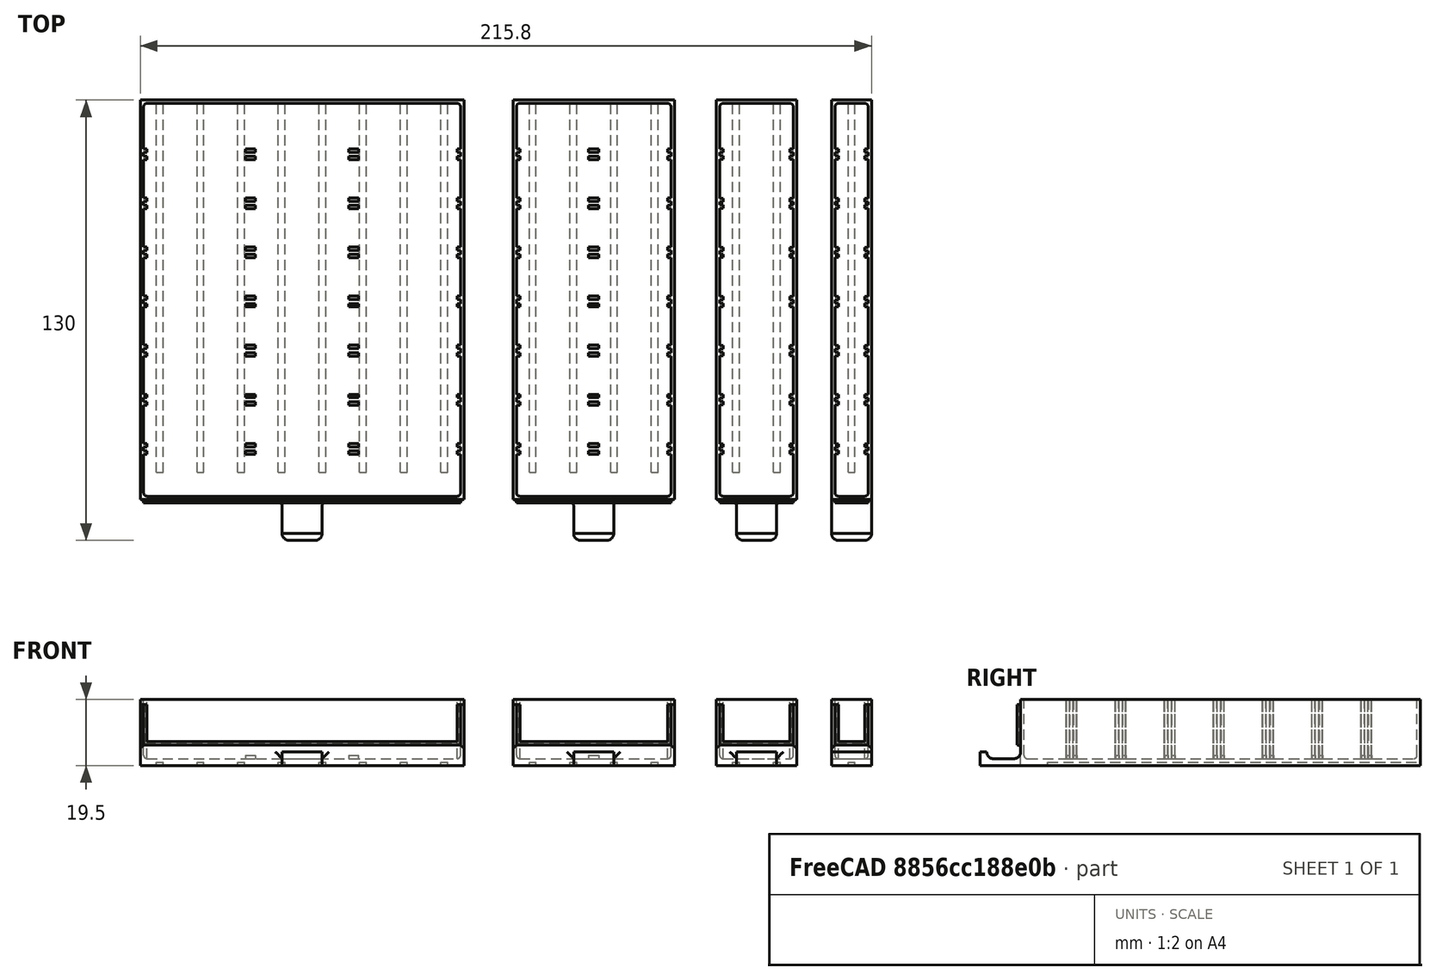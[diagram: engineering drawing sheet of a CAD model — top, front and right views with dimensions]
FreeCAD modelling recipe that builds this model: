
FCSTD DOCUMENT  (FreeCAD 0.16R)
Label: drawers
License: All rights reserved
LicenseURL: http://en.wikipedia.org/wiki/All_rights_reserved
objects: Part::Box×46, Part::Cut×23, Part::Fillet×20, Part::MultiFuse×19, Part::FeaturePython×8
note: 116 computed .brp shape members not serialized (recipe doc carries the construction recipe); baked Part::Feature solids carry a one-line shape summary decoded from their .brp

FEATURE [Part::Box] Box  label="outer_box"
  Height = 19.5
  Length = 95.5
  Width = 118
FEATURE [Part::Box] Box001  label="inner_box"
  Height = 18.5
  Length = 93.5
  Placement = pos=(1,1,2) rot=(0,0,1;0rad)
  Width = 116
FEATURE [Part::Fillet] Fillet
  Base = -> Box001
  Edges = 8 edges r=1: [Edge1,Edge3,Edge4,Edge5,Edge7,Edge8,Edge9,Edge11]
FEATURE [Part::Cut] Cut  label="Guideless Drawer"
  Base = -> Box
  Tool = -> Fillet
FEATURE [Part::Box] Box004  label="Guide"
  Height = 1
  Length = 2
  Placement = pos=(0,8,0) rot=(0,0,1;0rad)
  Width = 110
FEATURE [Part::FeaturePython] Array  label="Guide array"  # Draft array (typed FeaturePython)
  Angle = 360
  ArrayType = 0
  Axis = (0,0,1)
  Base = -> Box004
  Center = (0,0,0)
  Fuse = false
  IntervalAxis = (0,0,0)
  IntervalX = (12,0,0)
  IntervalY = (0,1,0)
  IntervalZ = (0,0,0)
  NumberPolar = 1
  NumberX = 8
  NumberY = 1
  NumberZ = 1
  Placement = pos=(4.75,0,0) rot=(0,0,1;0rad)
FEATURE [Part::Box] Box006  label="Separator Holder Block"
  Height = 17.5
  Length = 93.5
  Placement = pos=(1,13.4,2) rot=(0,0,1;0rad)
  Width = 3.2
FEATURE [Part::Box] Box007  label="Separator Gap"
  Height = 17.5
  Length = 93.5
  Placement = pos=(1,14.4,2) rot=(0,0,1;0rad)
  Width = 1.2
FEATURE [Part::Box] Box008  label="Separator Holder Gap Block"
  Height = 17.5
  Length = 91.5
  Placement = pos=(2,13.4,2) rot=(0,0,1;0rad)
  Width = 3.2
FEATURE [Part::Fillet] Fillet005
  Base = -> Box006
  Edges = 2 edges r=1: [Edge4,Edge8]
FEATURE [Part::Cut] Cut002  label="Separator Holder Guides"
  Base = -> Fillet005
  Tool = -> Box007
FEATURE [Part::Cut] Cut004  label="Handlerless Guided Drawer"
  Base = -> Cut
  Tool = -> Array
FEATURE [Part::Box] Box009  label="Bottom Separator Holder Gap Block"
  Height = 1
  Length = 3
  Placement = pos=(31,13.4,2) rot=(0,0,1;0rad)
  Width = 3.2
FEATURE [Part::FeaturePython] Array001  label="Bottom Separator Gap Array"  # Draft array (typed FeaturePython)
  Angle = 360
  ArrayType = 0
  Axis = (0,0,1)
  Base = -> Box009
  Center = (0,0,0)
  Fuse = false
  IntervalAxis = (0,0,0)
  IntervalX = (30.5,0,0)
  IntervalY = (0,1,0)
  IntervalZ = (0,0,0)
  NumberPolar = 1
  NumberX = 2
  NumberY = 1
  NumberZ = 1
FEATURE [Part::Cut] Cut005  label="Separator Holder Gap"
  Base = -> Box008
  Tool = -> Array001
FEATURE [Part::Cut] Cut006  label="Separator Holder"
  Base = -> Cut002
  Tool = -> Cut005
FEATURE [Part::FeaturePython] Array002  label="Separator Holder Array"  # Draft array (typed FeaturePython)
  Angle = 360
  ArrayType = 0
  Axis = (0,0,1)
  Base = -> Cut006
  Center = (0,0,0)
  Fuse = false
  IntervalAxis = (0,0,0)
  IntervalX = (1,0,0)
  IntervalY = (0,14.5,0)
  IntervalZ = (0,0,0)
  NumberPolar = 1
  NumberX = 1
  NumberY = 7
  NumberZ = 1
FEATURE [Part::Box] Box010  label="LabelHolder_Main_Block"
  Height = 12
  Length = 93.5
  Placement = pos=(1,-1,6) rot=(0,0,1;0rad)
  Width = 1
  expr: Placement.Base.y = outer_box.Placement.Base.y - LabelHolder_Main_Block.Width
  expr: Placement.Base.x = inner_box.Placement.Base.x
  expr: Length = inner_box.Length
FEATURE [Part::Box] Box011  label="LabelHolder_Inner_Gap"
  Height = 11.5
  Length = 92.5
  Placement = pos=(1.5,-0.5,6.5) rot=(0,0,1;0rad)
  Width = 0.5
  expr: Height = LabelHolder_Main_Block.Height - 0.5mm
  expr: Placement.Base.z = LabelHolder_Main_Block.Placement.Base.z + 0.5mm
  expr: Placement.Base.y = LabelHolder_Main_Block.Placement.Base.y + 0.5mm
  expr: Placement.Base.x = LabelHolder_Main_Block.Placement.Base.x + 0.5mm
  expr: Length = LabelHolder_Main_Block.Length - 1mm
FEATURE [Part::Box] Box012  label="LabelHolder_Outer_Gap"
  Height = 11
  Length = 91.5
  Placement = pos=(2,-1,7) rot=(0,0,1;0rad)
  Width = 0.5
  expr: Height = LabelHolder_Main_Block.Height - 1mm
  expr: Placement.Base.z = LabelHolder_Main_Block.Placement.Base.z + 1mm
  expr: Placement.Base.y = LabelHolder_Main_Block.Placement.Base.y
  expr: Placement.Base.x = LabelHolder_Main_Block.Placement.Base.x + 1mm
  expr: Length = LabelHolder_Main_Block.Length - 2mm
FEATURE [Part::MultiFuse] Fusion003  label="LabelHolder Gap"
  Shapes = -> [Box011,Box012]
FEATURE [Part::Cut] Cut007  label="LabelHolder"
  Base = -> Box010
  Tool = -> Fusion003
FEATURE [Part::MultiFuse] Fusion  label="Handlerless Drawer"
  Shapes = -> [Cut004,Array002]
FEATURE [Part::Box] Box013  label="Handler_block"
  Height = 2
  Length = 11.8
  Placement = pos=(41.85,-12,0) rot=(0,0,1;0rad)
  Width = 12
  expr: Placement.Base.y = outer_box.Placement.Base.y - Handler_block.Width
  expr: Placement.Base.x = outer_box.Placement.Base.x + (outer_box.Length - Handler_block.Length) / 2
FEATURE [Part::Box] Box015  label="Handler_pick"
  Height = 2
  Length = 11.8
  Placement = pos=(41.85,-12,2) rot=(0,0,1;0rad)
  Width = 2
  expr: Placement.Base.z = Handler_block.Placement.Base.z + 2mm
  expr: Placement.Base.y = Handler_block.Placement.Base.y
  expr: Placement.Base.x = Handler_block.Placement.Base.x
FEATURE [Part::MultiFuse] Fusion004
  Shapes = -> [Box015,Box013]
FEATURE [Part::Fillet] Fillet006
  Base = -> Fusion004
  Edges = 5 edges r=1.9: [Edge5,Edge8,Edge10,Edge13,Edge19]
FEATURE [Part::MultiFuse] Fusion005
  Shapes = -> [Fillet006,Fusion]
FEATURE [Part::Fillet] Fillet007  label="LabelHolderlessCabinet"
  Base = -> Fusion005
  Edges = 3 edges r=2: [Edge25,Edge34,Edge39]
FEATURE [Part::MultiFuse] Fusion006
  Shapes = -> [Cut007,Fillet007]
FEATURE [Part::Fillet] Fillet008  label="BigDrawer"
  Base = -> Fusion006
  Edges = 3 edges r=0.9: [Edge11,Edge27,Edge28]
FEATURE [Part::Box] Box016  label="outer_box001"
  Height = 19.5
  Length = 47.6
  Width = 118
FEATURE [Part::Box] Box017  label="inner_box001"
  Height = 18.5
  Length = 45.6
  Placement = pos=(1,1,2) rot=(0,0,1;0rad)
  Width = 116
FEATURE [Part::Fillet] Fillet009
  Base = -> Box017
  Edges = 8 edges r=1: [Edge1,Edge3,Edge4,Edge5,Edge7,Edge8,Edge9,Edge11]
FEATURE [Part::Cut] Cut008  label="Guideless drawer"
  Base = -> Box016
  Tool = -> Fillet009
FEATURE [Part::Box] Box018  label="Guide001"
  Height = 1
  Length = 2
  Placement = pos=(4.8,8,0) rot=(0,0,1;0rad)
  Width = 110
FEATURE [Part::FeaturePython] Array003  label="Guide Array"  # Draft array (typed FeaturePython)
  Angle = 360
  ArrayType = 0
  Axis = (0,0,1)
  Base = -> Box018
  Center = (0,0,0)
  Fuse = false
  IntervalAxis = (0,0,0)
  IntervalX = (12,0,0)
  IntervalY = (0,1,0)
  IntervalZ = (0,0,0)
  NumberPolar = 1
  NumberX = 4
  NumberY = 1
  NumberZ = 1
FEATURE [Part::Box] Box019  label="Separator Block"
  Height = 17.5
  Length = 45.6
  Placement = pos=(1,13.4,2) rot=(0,0,1;0rad)
  Width = 3.2
FEATURE [Part::Box] Box020  label="Separator Gap001"
  Height = 17.5
  Length = 45.6
  Placement = pos=(1,14.4,2) rot=(0,0,1;0rad)
  Width = 1.2
FEATURE [Part::Box] Box021  label="Separator Holder Gap Block001"
  Height = 17.5
  Length = 43.6
  Placement = pos=(2,13.4,2) rot=(0,0,1;0rad)
  Width = 3.2
FEATURE [Part::Fillet] Fillet010
  Base = -> Box019
  Edges = 2 edges r=1: [Edge4,Edge8]
FEATURE [Part::Cut] Cut009  label="Separator Holder Guides001"
  Base = -> Fillet010
  Tool = -> Box020
FEATURE [Part::Cut] Cut010  label="Separatorless Guided Drawer"
  Base = -> Cut008
  Tool = -> Array003
FEATURE [Part::Box] Box022  label="Bottom Separator Holder Gap Block001"
  Height = 1
  Length = 3
  Placement = pos=(22.3,13.4,2) rot=(0,0,1;0rad)
  Width = 3.2
FEATURE [Part::Cut] Cut011  label="Separator Holder Gap001"
  Base = -> Box021
  Tool = -> Box022
FEATURE [Part::Cut] Cut012  label="Separator Holder001"
  Base = -> Cut009
  Tool = -> Cut011
FEATURE [Part::FeaturePython] Array004  label="Separator Holder Array001"  # Draft array (typed FeaturePython)
  Angle = 360
  ArrayType = 0
  Axis = (0,0,1)
  Base = -> Cut012
  Center = (0,0,0)
  Fuse = false
  IntervalAxis = (0,0,0)
  IntervalX = (1,0,0)
  IntervalY = (0,14.5,0)
  IntervalZ = (0,0,0)
  NumberPolar = 1
  NumberX = 1
  NumberY = 7
  NumberZ = 1
FEATURE [Part::Box] Box023  label="LabelHolder_Main_Block001"
  Height = 12
  Length = 45.6
  Placement = pos=(1,-1,6) rot=(0,0,1;0rad)
  Width = 1
  expr: Placement.Base.y = outer_box.Placement.Base.y - LabelHolder_Main_Block.Width
  expr: Placement.Base.x = inner_box.Placement.Base.x
  expr: Length = inner_box.Length
FEATURE [Part::Box] Box024  label="LabelHolder_Inner_Gap001"
  Height = 11.5
  Length = 44.6
  Placement = pos=(1.5,-0.5,6.5) rot=(0,0,1;0rad)
  Width = 0.5
  expr: Placement.Base.y = LabelHolder_Main_Block.Placement.Base.y + 0.5mm
  expr: Height = LabelHolder_Main_Block.Height - 0.5mm
  expr: Placement.Base.z = LabelHolder_Main_Block.Placement.Base.z + 0.5mm
  expr: Length = inner_box.Length - 1mm
FEATURE [Part::Box] Box025  label="LabelHolder_Outer_Gap001"
  Height = 11
  Length = 43.6
  Placement = pos=(2,-1,7) rot=(0,0,1;0rad)
  Width = 0.5
  expr: Placement.Base.y = LabelHolder_Main_Block.Placement.Base.y
  expr: Placement.Base.x = LabelHolder_Main_Block.Placement.Base.x + 1mm
  expr: Length = LabelHolder_Main_Block.Length - 2mm
  expr: Height = LabelHolder_Main_Block.Height - 1mm
  expr: Placement.Base.z = LabelHolder_Main_Block.Placement.Base.z + 1mm
FEATURE [Part::MultiFuse] Fusion007  label="LabelHolder_Gap"
  Shapes = -> [Box024,Box025]
FEATURE [Part::Cut] Cut013  label="LabelHolder001"
  Base = -> Box023
  Tool = -> Fusion007
FEATURE [Part::MultiFuse] Fusion008  label="Handlerless Drawer001"
  Shapes = -> [Array004,Cut010]
FEATURE [Part::Box] Box026  label="Handler_block001"
  Height = 2
  Length = 11.8
  Placement = pos=(17.9,-12,0) rot=(0,0,1;0rad)
  Width = 12
  expr: Placement.Base.y = outer_box.Placement.Base.y - Handler_block.Width
  expr: Placement.Base.x = outer_box.Placement.Base.x + (outer_box.Length - Handler_block.Length) / 2
FEATURE [Part::Box] Box027  label="Handler_pick001"
  Height = 2
  Length = 11.8
  Placement = pos=(17.9,-12,2) rot=(0,0,1;0rad)
  Width = 2
  expr: Placement.Base.z = Handler_block.Placement.Base.z + 2mm
  expr: Placement.Base.y = Handler_block.Placement.Base.y
  expr: Placement.Base.x = Handler_block.Placement.Base.x
FEATURE [Part::MultiFuse] Fusion009
  Shapes = -> [Box026,Box027]
FEATURE [Part::Fillet] Fillet011
  Base = -> Fusion009
  Edges = 5 edges r=1.9: [Edge5,Edge11,Edge15,Edge18,Edge19]
FEATURE [Part::MultiFuse] Fusion010
  Shapes = -> [Fusion008,Fillet011]
FEATURE [Part::Fillet] Fillet012
  Base = -> Fusion010
  Edges = 3 edges r=2: [Edge627,Edge628,Edge629]
FEATURE [Part::MultiFuse] Fusion011
  Shapes = -> [Fillet012,Cut013]
FEATURE [Part::Fillet] Fillet013  label="StandardDrawer"
  Base = -> Fusion011
  Edges = 3 edges r=0.9: [Edge31,Edge32,Edge38]
  Placement = pos=(110,0,0) rot=(0,0,1;0rad)
FEATURE [Part::Box] Box028  label="outer_box002"
  Height = 19.5
  Length = 23.7
  Width = 118
FEATURE [Part::Box] Box029  label="inner_box002"
  Height = 18.5
  Length = 21.7
  Placement = pos=(1,1,2) rot=(0,0,1;0rad)
  Width = 116
FEATURE [Part::Fillet] Fillet014  label="Filleted Inner Box"
  Base = -> Box029
  Edges = 8 edges r=1: [Edge1,Edge3,Edge4,Edge5,Edge7,Edge8,Edge9,Edge11]
FEATURE [Part::Cut] Cut014  label="Guideless Drawer001"
  Base = -> Box028
  Tool = -> Fillet014
FEATURE [Part::Box] Box030  label="Guide002"
  Height = 1
  Length = 2
  Placement = pos=(0,8,0) rot=(0,0,1;0rad)
  Width = 110
FEATURE [Part::FeaturePython] Array005  label="Guide array001"  # Draft array (typed FeaturePython)
  Angle = 360
  ArrayType = 0
  Axis = (0,0,1)
  Base = -> Box030
  Center = (0,0,0)
  Fuse = false
  IntervalAxis = (0,0,0)
  IntervalX = (12,0,0)
  IntervalY = (0,1,0)
  IntervalZ = (0,0,0)
  NumberPolar = 1
  NumberX = 2
  NumberY = 1
  NumberZ = 1
  Placement = pos=(4.85,0,0) rot=(0,0,1;0rad)
FEATURE [Part::Box] Box031  label="Separator Holder Gap002"
  Height = 17.5
  Length = 21.7
  Placement = pos=(1,14.5,2) rot=(0,0,1;0rad)
  Width = 1
FEATURE [Part::Box] Box032  label="Separator Block001"
  Height = 17.5
  Length = 21.7
  Placement = pos=(1,13.5,2) rot=(0,0,1;0rad)
  Width = 3
FEATURE [Part::Fillet] Fillet015  label="Filletted Separator Block"
  Base = -> Box032
  Edges = 2 edges r=1: [Edge4,Edge8]
FEATURE [Part::Box] Box033  label="Separator Gap002"
  Height = 17.5
  Length = 19.7
  Placement = pos=(2,13.5,2) rot=(0,0,1;0rad)
  Width = 3
FEATURE [Part::Cut] Cut015
  Base = -> Fillet015
  Tool = -> Box033
FEATURE [Part::Cut] Cut003  label="Separator Holder002"
  Base = -> Cut015
  Tool = -> Box031
FEATURE [Part::FeaturePython] Array006  label="Separator Holders Array"  # Draft array (typed FeaturePython)
  Angle = 360
  ArrayType = 0
  Axis = (0,0,1)
  Base = -> Cut003
  Center = (0,0,0)
  Fuse = false
  IntervalAxis = (0,0,0)
  IntervalX = (1,0,0)
  IntervalY = (0,14.5,0)
  IntervalZ = (0,0,0)
  NumberPolar = 1
  NumberX = 1
  NumberY = 7
  NumberZ = 1
FEATURE [Part::Cut] Cut016  label="Guided Drawer"
  Base = -> Cut014
  Tool = -> Array005
FEATURE [Part::Box] Box034  label="LabelHolder_Main_Block002"
  Height = 12
  Length = 21.7
  Placement = pos=(1,-1,6) rot=(0,0,1;0rad)
  Width = 1
  expr: Length = inner_box.Length
  expr: Placement.Base.x = inner_box.Placement.Base.x
  expr: Placement.Base.y = outer_box.Placement.Base.y - LabelHolder_Main_Block.Width
FEATURE [Part::Box] Box035  label="LabelHolder_Inner_Gap002"
  Height = 11.5
  Length = 20.7
  Placement = pos=(1.5,-0.5,6.5) rot=(0,0,1;0rad)
  Width = 0.5
  expr: Length = LabelHolder_Main_Block.Length - 1mm
  expr: Placement.Base.x = LabelHolder_Main_Block.Placement.Base.x + (LabelHolder_Main_Block.Length - LabelHolder_Inner_Gap.Length) / 2
  expr: Placement.Base.y = LabelHolder_Main_Block.Placement.Base.y + LabelHolder_Inner_Gap.Width
  expr: Width = LabelHolder_Main_Block.Width / 2
  expr: Height = LabelHolder_Main_Block.Height - 0.5mm
  expr: Placement.Base.z = LabelHolder_Main_Block.Placement.Base.z + 0.5mm
FEATURE [Part::Box] Box036  label="LabelHolder_Outer_Gap002"
  Height = 11
  Length = 19.7
  Placement = pos=(2,-1,7) rot=(0,0,1;0rad)
  Width = 0.5
  expr: Placement.Base.y = LabelHolder_Inner_Gap.Placement.Base.y - LabelHolder_Outer_Gap.Width
  expr: Placement.Base.x = LabelHolder_Main_Block.Placement.Base.x + (LabelHolder_Main_Block.Length - LabelHolder_Outer_Gap.Length) / 2
  expr: Placement.Base.z = LabelHolder_Main_Block.Placement.Base.z + 1mm
  expr: Height = LabelHolder_Main_Block.Height - 1mm
  expr: Width = LabelHolder_Main_Block.Width / 2
  expr: Length = LabelHolder_Main_Block.Length - 2mm
FEATURE [Part::MultiFuse] Fusion012  label="LabelHolder_Gap001"
  Shapes = -> [Box035,Box036]
FEATURE [Part::Cut] Cut017  label="LabelHolder002"
  Base = -> Box034
  Tool = -> Fusion012
FEATURE [Part::MultiFuse] Fusion013  label="Handlerless Drawer002"
  Shapes = -> [Cut016,Array006]
FEATURE [Part::Box] Box037  label="Handler_block002"
  Height = 2
  Length = 11.8
  Placement = pos=(5.95,-12,0) rot=(0,0,1;0rad)
  Width = 12
  expr: Placement.Base.x = (outer_box.Length - Handler_block.Length) / 2
FEATURE [Part::Box] Box014  label="Handler_pick002"
  Height = 2
  Length = 11.8
  Placement = pos=(5.95,-12,2) rot=(0,0,1;0rad)
  Width = 2
  expr: Placement.Base.z = Handler_block.Placement.Base.z + 2mm
  expr: Placement.Base.y = Handler_block.Placement.Base.y
  expr: Placement.Base.x = Handler_block.Placement.Base.x
FEATURE [Part::MultiFuse] Fusion014
  Shapes = -> [Box014,Box037]
FEATURE [Part::Fillet] Fillet016  label="Handler"
  Base = -> Fusion014
  Edges = 5 edges r=1.9: [Edge5,Edge8,Edge10,Edge13,Edge19]
FEATURE [Part::MultiFuse] Fusion015
  Shapes = -> [Fusion013,Fillet016]
FEATURE [Part::Fillet] Fillet017  label="LabelHolderlessDrawer"
  Base = -> Fusion015
  Edges = 3 edges r=2: [Edge6,Edge7,Edge8]
FEATURE [Part::MultiFuse] Fusion016
  Shapes = -> [Cut017,Fillet017]
FEATURE [Part::Fillet] Fillet018  label="SmallDrawer"
  Base = -> Fusion016
  Edges = 3 edges r=0.9: [Edge11,Edge27,Edge28]
  Placement = pos=(170,0,0) rot=(0,0,1;0rad)
FEATURE [Part::Box] Box038  label="outer_box003"
  Height = 19.5
  Length = 11.8
  Width = 118
FEATURE [Part::Box] Box039  label="inner_box003"
  Height = 17.5
  Length = 9.8
  Placement = pos=(1,1,2) rot=(0,0,1;0rad)
  Width = 116
FEATURE [Part::Fillet] Fillet019
  Base = -> Box039
  Edges = 8 edges r=1: [Edge1,Edge3,Edge4,Edge5,Edge7,Edge8,Edge9,Edge11]
FEATURE [Part::Cut] Cut018  label="Guideless Drawer002"
  Base = -> Box038
  Tool = -> Fillet019
FEATURE [Part::Box] Box040  label="Guide003"
  Height = 1
  Length = 2
  Placement = pos=(4.9,8,0) rot=(0,0,1;0rad)
  Width = 110
FEATURE [Part::Box] Box041  label="Separator Holder Block Draft"
  Height = 17.5
  Length = 9.8
  Width = 3
FEATURE [Part::Box] Box042  label="Separator Gap003"
  Height = 17.5
  Length = 9.8
  Placement = pos=(0,1,0) rot=(0,0,1;0rad)
  Width = 1
FEATURE [Part::Box] Box043  label="Separator Holder Gap003"
  Height = 17.5
  Length = 7.8
  Placement = pos=(1,0,0) rot=(0,0,1;0rad)
  Width = 3
FEATURE [Part::Fillet] Fillet020
  Base = -> Box041
  Edges = 2 edges r=1: [Edge4,Edge8]
FEATURE [Part::Cut] Cut019
  Base = -> Fillet020
  Tool = -> Box042
FEATURE [Part::Cut] Cut020  label="Separator Holder Draft"
  Base = -> Cut019
  Tool = -> Box043
FEATURE [Part::FeaturePython] Array007  label="Separator Holder Array002"  # Draft array (typed FeaturePython)
  Angle = 360
  ArrayType = 0
  Axis = (0,0,1)
  Base = -> Cut020
  Center = (0,0,0)
  Fuse = false
  IntervalAxis = (0,0,0)
  IntervalX = (1,0,0)
  IntervalY = (0,14.5,0)
  IntervalZ = (0,0,0)
  NumberPolar = 1
  NumberX = 1
  NumberY = 7
  NumberZ = 1
  Placement = pos=(1,13.5,2) rot=(0,0,1;0rad)
FEATURE [Part::Cut] Cut021  label="Guided Separatorless Drawer"
  Base = -> Cut018
  Tool = -> Box040
FEATURE [Part::Box] Box044  label="labelholder_main_block"
  Height = 12
  Length = 9.8
  Placement = pos=(1,-1,6) rot=(0,0,1;0rad)
  Width = 1
FEATURE [Part::Box] Box045  label="labelholder_inner_gap"
  Height = 11.5
  Length = 8.8
  Placement = pos=(1.5,-0.5,6.5) rot=(0,0,1;0rad)
  Width = 0.5
  expr: Height = labelholder_main_block.Height - 0.5mm
  expr: Placement.Base.z = labelholder_main_block.Placement.Base.z + 0.5mm
FEATURE [Part::Box] Box046  label="LabelHolder Outer Gap"
  Height = 11
  Length = 7.8
  Placement = pos=(2,-1,7) rot=(0,0,1;0rad)
  Width = 0.5
  expr: Height = labelholder_main_block.Height - 1mm
  expr: Placement.Base.z = labelholder_main_block.Placement.Base.z + 1mm
FEATURE [Part::Cut] Cut022
  Base = -> Box044
  Tool = -> Box045
FEATURE [Part::Cut] Cut023  label="Label Holder"
  Base = -> Cut022
  Tool = -> Box046
FEATURE [Part::MultiFuse] Fusion017  label="Separator Holdered Drawer"
  Shapes = -> [Cut021,Array007]
FEATURE [Part::Box] Box047  label="HandlerBlock"
  Height = 2
  Length = 11.8
  Placement = pos=(0,-12,0) rot=(0,0,1;0rad)
  Width = 12
FEATURE [Part::Box] Box048  label="Cube"
  Height = 2
  Length = 11.8
  Placement = pos=(0,-12,2) rot=(0,0,1;0rad)
  Width = 2
FEATURE [Part::MultiFuse] Fusion001
  Shapes = -> [Box048,Box047]
FEATURE [Part::Fillet] Fillet021
  Base = -> Fusion001
  Edges = 5 edges r=1.9: [Edge5,Edge8,Edge10,Edge13,Edge19]
FEATURE [Part::MultiFuse] Fusion002
  Shapes = -> [Fillet021,Fusion017]
FEATURE [Part::Fillet] Fillet022
  Base = -> Fusion002
  Edges = 1 edges r=2: [Edge42]
FEATURE [Part::MultiFuse] Fusion018
  Shapes = -> [Cut023,Fillet022]
FEATURE [Part::Fillet] Fillet023  label="TinyDrawer"
  Base = -> Fusion018
  Edges = 3 edges r=0.9: [Edge11,Edge27,Edge28]
  Placement = pos=(204,0,0) rot=(0,0,1;0rad)
